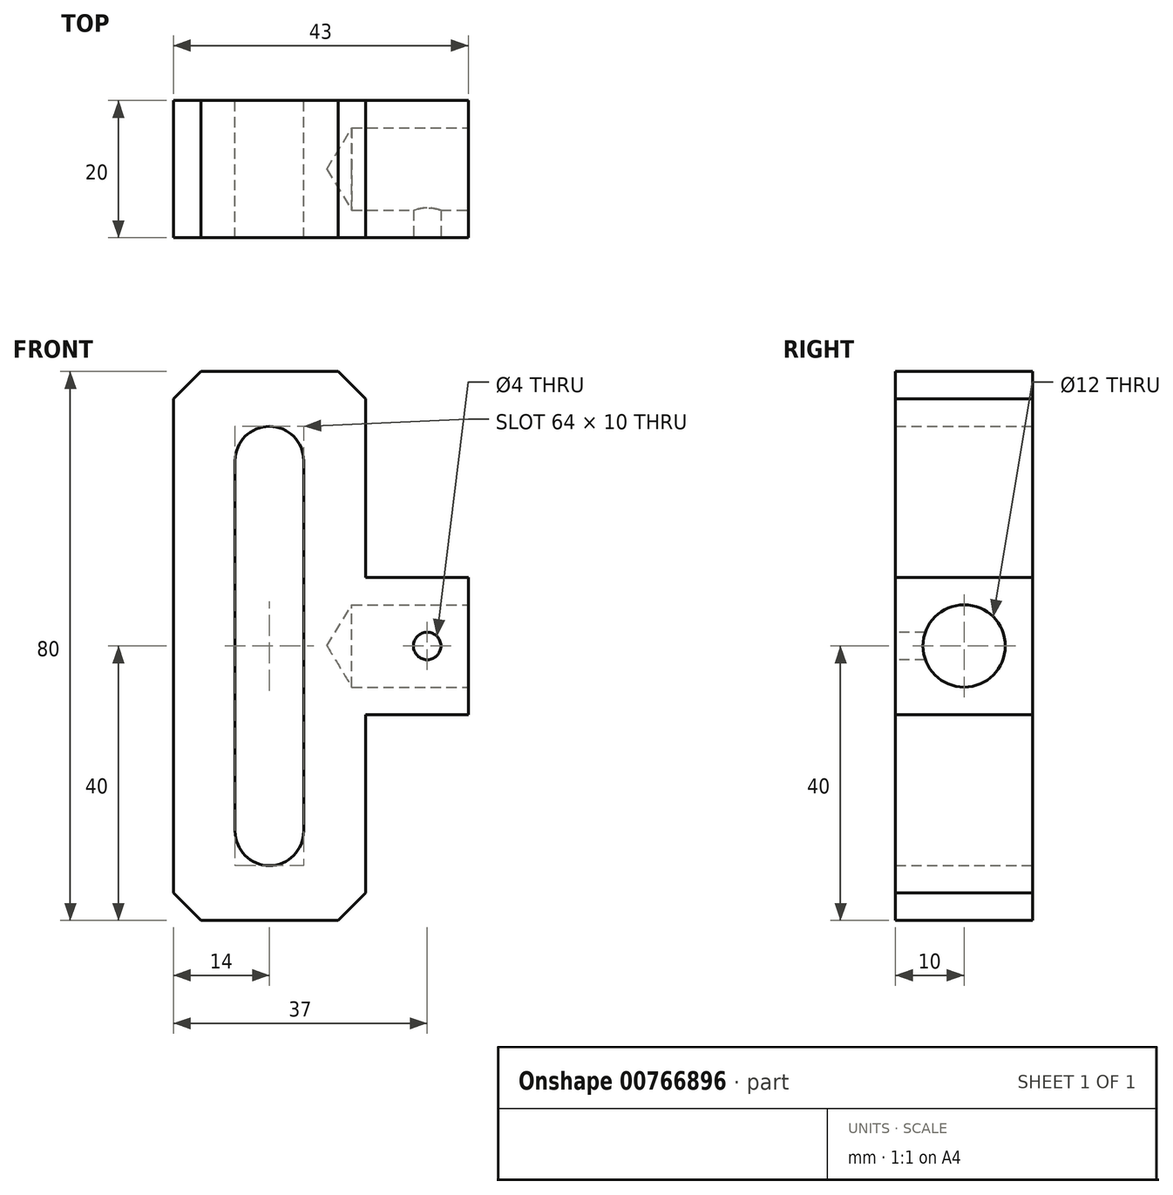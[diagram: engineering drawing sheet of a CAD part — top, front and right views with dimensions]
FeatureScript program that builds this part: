
annotation { "Feature Type Name" : "Feature", "Feature Type Description" : "" }
export const myFeature = defineFeature(function(context is Context, id is Id, definition is map)
    precondition{}
    {
        {
            var Q0;
            Q0=qCreatedBy(makeId("Front.planeOp"),FACE);
            var sketch = newSketch(context, id + "F0", { "sketchPlane" : qUnion([Q0])});
            skLineSegment(sketch, "E0.bottom", {"start": v(-14, -40) * mm, "end": v(14, -40) * mm});
            skLineSegment(sketch, "E0.top", {"start": v(-14, 40) * mm, "end": v(14, 40) * mm});
            skLineSegment(sketch, "E0.left", {"start": v(-14, -40) * mm, "end": v(-14, 40) * mm});
            skLineSegment(sketch, "E0.right", {"start": v(14, -40) * mm, "end": v(14, -10) * mm});
            skLineSegment(sketch, "E1", {"start": v(14, -10) * mm, "end": v(29, -10) * mm});
            skLineSegment(sketch, "E2", {"start": v(29, -10) * mm, "end": v(29, 10) * mm});
            skLineSegment(sketch, "E3", {"start": v(29, 10) * mm, "end": v(14, 10) * mm});
            skLineSegment(sketch, "E4.trimOffspring", {"start": v(14, 10) * mm, "end": v(14, 40) * mm});
            skArc(sketch, "E5", {"start": v(5, 27) * mm, "mid": v(0, 32) * mm, "end": v(-5, 27) * mm});
            skArc(sketch, "E6", {"start": v(-5, -27) * mm, "mid": v(0, -32) * mm, "end": v(5, -27) * mm});
            skLineSegment(sketch, "E7", {"start": v(-5, 27) * mm, "end": v(-5, -27) * mm});
            skLineSegment(sketch, "E8", {"start": v(5, -27) * mm, "end": v(5, 27) * mm});
            skSolve(sketch);
        }
        {
            var Q0;
            Q0=makeQuery(id+"F0.imprint","IMPRINT",FACE,{"disambiguationData":[TD([[makeQuery(id+"F0.imprint","IMPRINT",EDGE,{"derivedFrom":sQuery(id+"F0.wireOp",EDGE,"E0.bottom")}),1.0]])]});
            extrude(context, id + "F1", {"entities" : qUnion([Q0]), "depth" : 10 * mm, "offsetDistance" : 25 * mm, "hasSecondDirection" : true, "secondDirectionOppositeDirection" : true, "secondDirectionDepth" : 10 * mm});
        }
        {
            var Q0;
            Q0=makeQuery(id+"F1.opExtrude","SWEPT_EDGE",EDGE,{"disambiguationData":[OSD([sQuery(id+"F0.wireOp",EDGE,"E0.top"),sQuery(id+"F0.wireOp",EDGE,"E4.trimOffspring")])]});
            var Q1;
            Q1=makeQuery(id+"F1.opExtrude","SWEPT_EDGE",EDGE,{"disambiguationData":[OSD([sQuery(id+"F0.wireOp",EDGE,"E0.top"),sQuery(id+"F0.wireOp",EDGE,"E0.left")])]});
            var Q2;
            Q2=makeQuery(id+"F1.opExtrude","SWEPT_EDGE",EDGE,{"disambiguationData":[OSD([sQuery(id+"F0.wireOp",EDGE,"E0.bottom"),sQuery(id+"F0.wireOp",EDGE,"E0.right")])]});
            var Q3;
            Q3=makeQuery(id+"F1.opExtrude","SWEPT_EDGE",EDGE,{"disambiguationData":[OSD([sQuery(id+"F0.wireOp",EDGE,"E0.bottom"),sQuery(id+"F0.wireOp",EDGE,"E0.left")])]});
            chamfer(context, id + "F2", {"entities" : qUnion([Q0, Q1, Q2, Q3]), "width" : 4 * mm, "tangentPropagation" : true});
        }
        {
            var Q0;
            Q0=makeQuery(id+"F1.opExtrude","CAP_FACE",FACE,{"disambiguationData":[OSD([sQuery(id+"F0.wireOp",EDGE,"E0.bottom"),sQuery(id+"F0.wireOp",EDGE,"E0.top"),sQuery(id+"F0.wireOp",EDGE,"E0.left"),sQuery(id+"F0.wireOp",EDGE,"E0.right"),sQuery(id+"F0.wireOp",EDGE,"E1"),sQuery(id+"F0.wireOp",EDGE,"E2"),sQuery(id+"F0.wireOp",EDGE,"E3"),sQuery(id+"F0.wireOp",EDGE,"E4.trimOffspring"),sQuery(id+"F0.wireOp",EDGE,"E5"),sQuery(id+"F0.wireOp",EDGE,"E6"),sQuery(id+"F0.wireOp",EDGE,"E7"),sQuery(id+"F0.wireOp",EDGE,"E8")])],"isStart":false});
            var sketch = newSketch(context, id + "F3", { "sketchPlane" : qUnion([Q0])});
            skPoint(sketch, "E9", {"position": v(23, 0) * mm});
            skSolve(sketch);
        }
        {
            var Q0;
            Q0=sQuery(id+"F3.wireOp",VERTEX,"E9");
            var Q1;
            Q1=makeQuery(id+"F1.opExtrude","SWEPT_BODY",BODY,{"disambiguationData":[OSD([sQuery(id+"F0.wireOp",EDGE,"E0.bottom"),sQuery(id+"F0.wireOp",EDGE,"E0.top"),sQuery(id+"F0.wireOp",EDGE,"E0.left"),sQuery(id+"F0.wireOp",EDGE,"E0.right"),sQuery(id+"F0.wireOp",EDGE,"E1"),sQuery(id+"F0.wireOp",EDGE,"E2"),sQuery(id+"F0.wireOp",EDGE,"E3"),sQuery(id+"F0.wireOp",EDGE,"E4.trimOffspring"),sQuery(id+"F0.wireOp",EDGE,"E5"),sQuery(id+"F0.wireOp",EDGE,"E6"),sQuery(id+"F0.wireOp",EDGE,"E7"),sQuery(id+"F0.wireOp",EDGE,"E8")])]});
            hole(context, id + "F4", {"style" : HoleStyle.SIMPLE, "endStyle" : HoleEndStyle.BLIND, "holeDiameter" : 4 * mm, "majorDiameter" : 5 * mm, "holeDepth" : 10 * mm, "isTappedThrough" : true, "tappedDepth" : 12 * mm, "tapClearance" : 3, "locations" : qUnion([Q0]), "scope" : qUnion([Q1])});
        }
        {
            var Q0;
            Q0=makeQuery(id+"F1.opExtrude","SWEPT_FACE",FACE,{"disambiguationData":[OSD([sQuery(id+"F0.wireOp",EDGE,"E2")])]});
            var sketch = newSketch(context, id + "F5", { "sketchPlane" : qUnion([Q0])});
            skPoint(sketch, "E10", {"position": v(0, 0) * mm});
            skSolve(sketch);
        }
        {
            var Q0;
            Q0=sQuery(id+"F5.wireOp",VERTEX,"E10");
            var Q1;
            Q1=makeQuery(id+"F1.opExtrude","SWEPT_BODY",BODY,{"disambiguationData":[OSD([sQuery(id+"F0.wireOp",EDGE,"E0.bottom"),sQuery(id+"F0.wireOp",EDGE,"E0.top"),sQuery(id+"F0.wireOp",EDGE,"E0.left"),sQuery(id+"F0.wireOp",EDGE,"E0.right"),sQuery(id+"F0.wireOp",EDGE,"E1"),sQuery(id+"F0.wireOp",EDGE,"E2"),sQuery(id+"F0.wireOp",EDGE,"E3"),sQuery(id+"F0.wireOp",EDGE,"E4.trimOffspring"),sQuery(id+"F0.wireOp",EDGE,"E5"),sQuery(id+"F0.wireOp",EDGE,"E6"),sQuery(id+"F0.wireOp",EDGE,"E7"),sQuery(id+"F0.wireOp",EDGE,"E8")])]});
            hole(context, id + "F6", {"style" : HoleStyle.SIMPLE, "endStyle" : HoleEndStyle.BLIND, "holeDiameter" : 12 * mm, "majorDiameter" : 5 * mm, "holeDepth" : 17 * mm, "isTappedThrough" : true, "tappedDepth" : 12 * mm, "tapClearance" : 3, "locations" : qUnion([Q0]), "scope" : qUnion([Q1])});
        }
    });
